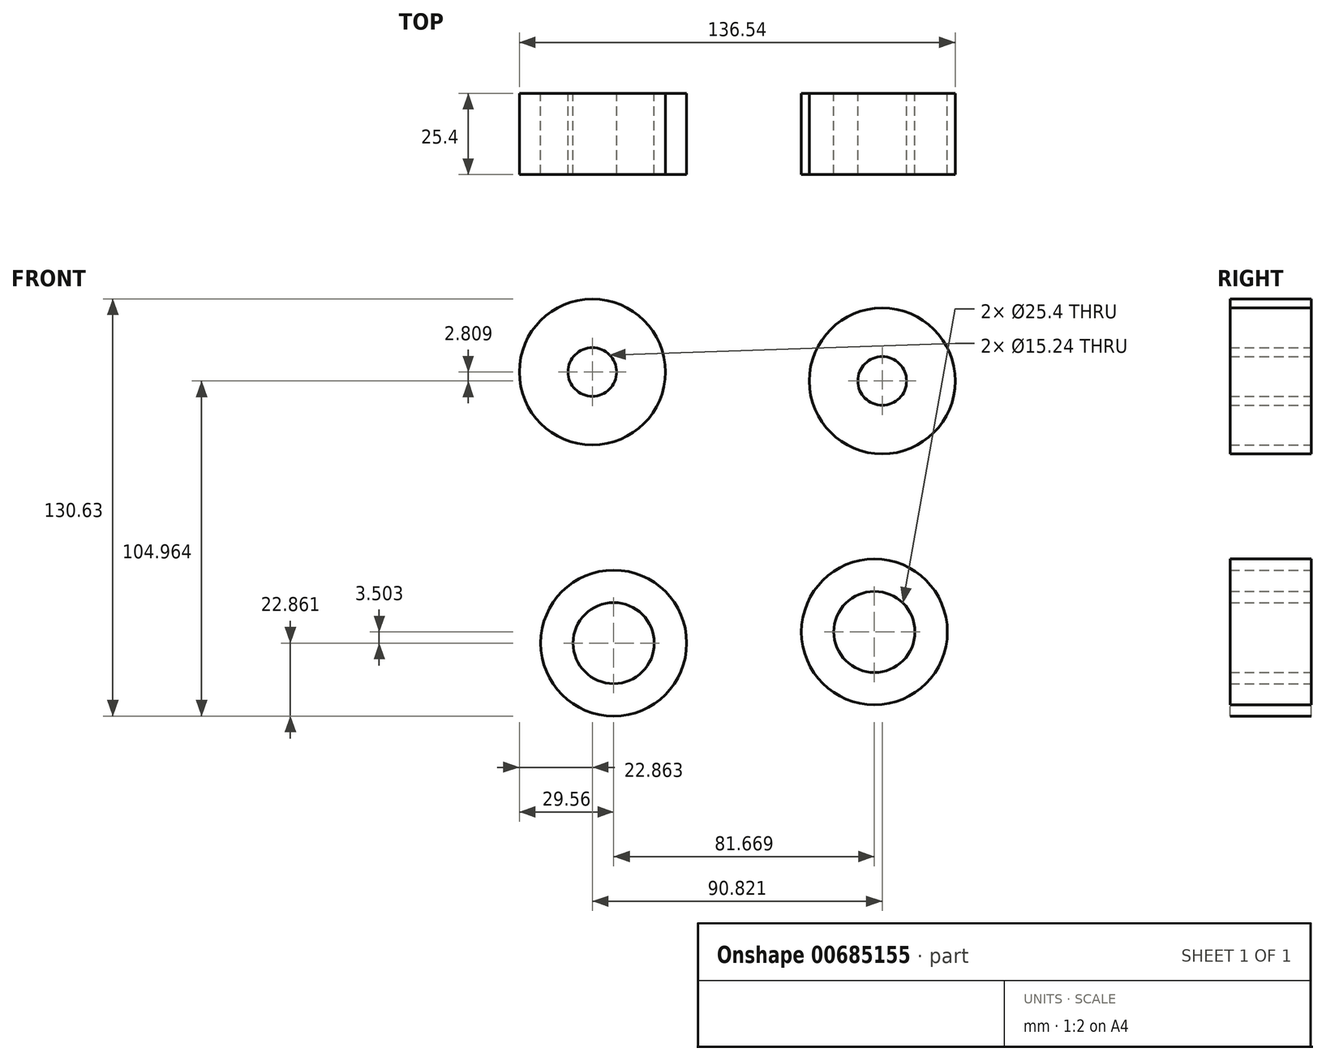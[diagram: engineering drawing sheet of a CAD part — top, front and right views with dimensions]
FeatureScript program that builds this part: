
annotation { "Feature Type Name" : "Feature", "Feature Type Description" : "" }
export const myFeature = defineFeature(function(context is Context, id is Id, definition is map)
    precondition{}
    {
        {
            var Q0;
            Q0=qCreatedBy(makeId("Front.planeOp"),FACE);
            var sketch = newSketch(context, id + "F0", { "sketchPlane" : qUnion([Q0])});
            skCircle(sketch, "E0", {"center": v(-46.06, 42.6) * mm, "radius": 22.86 * mm});
            skCircle(sketch, "E1", {"center": v(44.76, 39.8) * mm, "radius": 22.86 * mm});
            skCircle(sketch, "E2", {"center": v(42.3, -38.8) * mm, "radius": 22.86 * mm});
            skCircle(sketch, "E3", {"center": v(-46.06, 42.6) * mm, "radius": 7.62 * mm});
            skCircle(sketch, "E4", {"center": v(44.76, 39.8) * mm, "radius": 7.62 * mm});
            skCircle(sketch, "E5", {"center": v(42.3, -38.8) * mm, "radius": 12.7 * mm});
            skCircle(sketch, "E6", {"center": v(-39.36, -42.3) * mm, "radius": 22.86 * mm});
            skCircle(sketch, "E7", {"center": v(-39.36, -42.3) * mm, "radius": 12.7 * mm});
            skSolve(sketch);
        }
        {
            var Q0;
            Q0 = qSketchRegion(id + "F0", true);
            extrude(context, id + "F1", {"entities" : qUnion([Q0]), "depth" : 25.4 * mm, "offsetDistance" : 25.4 * mm});
        }
    });
